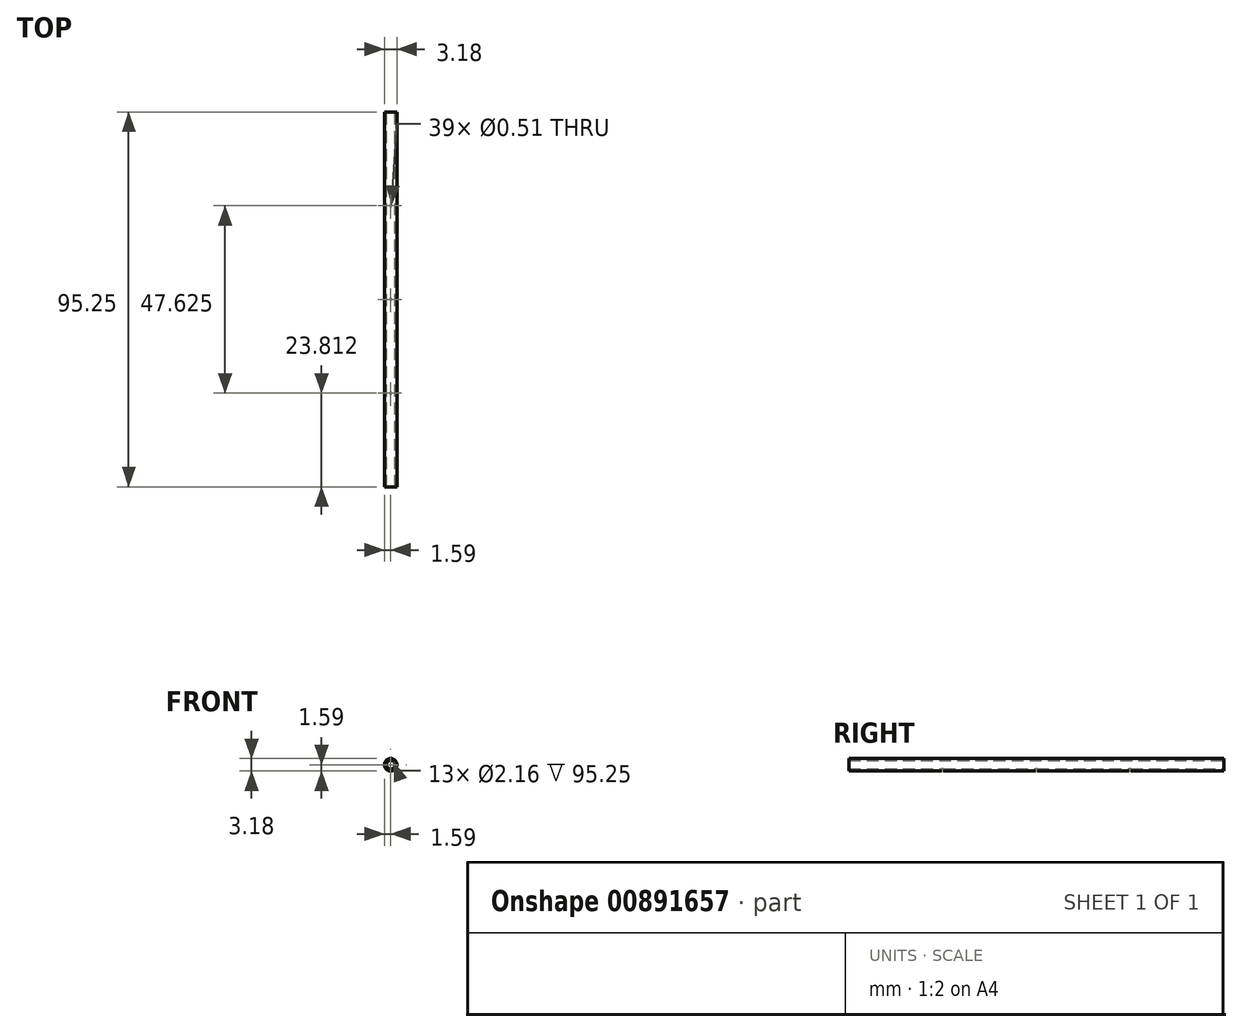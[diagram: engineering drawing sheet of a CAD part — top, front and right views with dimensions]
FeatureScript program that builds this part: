
annotation { "Feature Type Name" : "Feature", "Feature Type Description" : "" }
export const myFeature = defineFeature(function(context is Context, id is Id, definition is map)
    precondition{}
    {
        {
            var Q0;
            Q0=qCreatedBy(makeId("Front.planeOp"),FACE);
            var sketch = newSketch(context, id + "F0", { "sketchPlane" : qUnion([Q0])});
            skCircle(sketch, "E0", {"center": v(0, 0) * mm, "radius": 1.59 * mm});
            skCircle(sketch, "E1", {"center": v(0, 0) * mm, "radius": 1.08 * mm});
            skSolve(sketch);
        }
        {
            var Q0;
            Q0=makeQuery(id+"F0.imprint","IMPRINT",FACE,{"disambiguationData":[TD([[makeQuery(id+"F0.imprint","IMPRINT",EDGE,{"derivedFrom":sQuery(id+"F0.wireOp",EDGE,"E0")}),1.0]])]});
            extrude(context, id + "F1", {"entities" : qUnion([Q0]), "depth" : 95.25 * mm, "offsetDistance" : 25.4 * mm});
        }
        {
            var Q0;
            Q0=qCreatedBy(makeId("Top.planeOp"),FACE);
            var sketch = newSketch(context, id + "F2", { "sketchPlane" : qUnion([Q0])});
            skCircle(sketch, "E2", {"center": v(0, -71.44) * mm, "radius": 0.25 * mm});
            skCircle(sketch, "E3", {"center": v(0, -23.81) * mm, "radius": 0.25 * mm});
            skCircle(sketch, "E4", {"center": v(0, -47.63) * mm, "radius": 0.25 * mm});
            skSolve(sketch);
        }
        {
            var Q0;
            Q0 = qSketchRegion(id + "F2", true);
            extrude(context, id + "F3", {"entities" : qUnion([Q0]), "operationType" : NewBodyOperationType.REMOVE, "endBound" : BoundingType.THROUGH_ALL, "oppositeDirection" : true, "depth" : 25.4 * mm, "offsetDistance" : 25.4 * mm});
        }
    });
